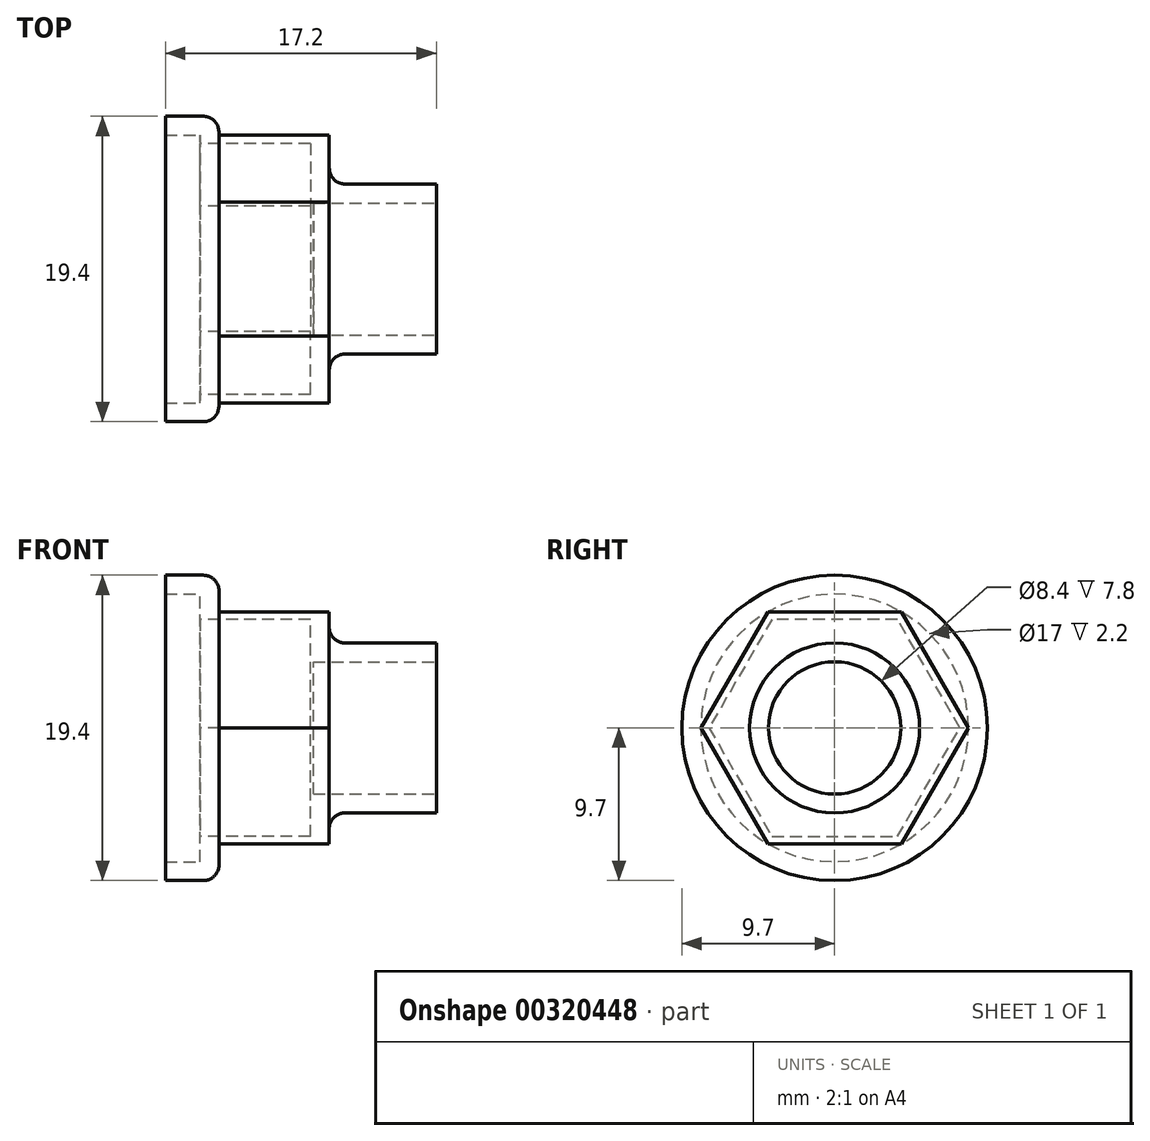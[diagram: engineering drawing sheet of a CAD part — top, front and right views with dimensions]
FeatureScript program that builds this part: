
annotation { "Feature Type Name" : "Feature", "Feature Type Description" : "" }
export const myFeature = defineFeature(function(context is Context, id is Id, definition is map)
    precondition{}
    {
        {
            var Q0;
            Q0=qCreatedBy(makeId("Top.planeOp"),FACE);
            var sketch = newSketch(context, id + "F0", { "sketchPlane" : qUnion([Q0])});
            skLineSegment(sketch, "E0", {"start": v(0, 6.7) * mm, "end": v(7, 6.7) * mm});
            skLineSegment(sketch, "E1", {"start": v(7, 6.7) * mm, "end": v(7, 4.2) * mm});
            skLineSegment(sketch, "E2", {"start": v(7, 4.2) * mm, "end": v(15, 4.2) * mm});
            skLineSegment(sketch, "E3", {"start": v(15, 4.2) * mm, "end": v(15, 4.2) * mm});
            skArc(sketch, "E4", {"start": v(19.2, 0) * mm, "mid": v(17.97, 2.97) * mm, "end": v(15, 4.2) * mm, "construction": true});
            skLineSegment(sketch, "E5", {"start": v(0, 6.7) * mm, "end": v(0, 8.5) * mm});
            skLineSegment(sketch, "E6", {"start": v(0, 8.5) * mm, "end": v(-2.2, 8.5) * mm});
            skLineSegment(sketch, "E7", {"start": v(19.2, 0) * mm, "end": v(0, 0) * mm, "construction": true});
            skLineSegment(sketch, "E8", {"start": v(-2.2, 8.5) * mm, "end": v(-2.2, 9.7) * mm});
            skLineSegment(sketch, "E9", {"start": v(-2.2, 9.7) * mm, "end": v(1.2, 9.7) * mm});
            skLineSegment(sketch, "E10", {"start": v(1.2, 9.7) * mm, "end": v(1.2, 8.5) * mm});
            skLineSegment(sketch, "E11", {"start": v(1.2, 8.5) * mm, "end": v(8.2, 8.5) * mm});
            skLineSegment(sketch, "E12", {"start": v(8.2, 8.5) * mm, "end": v(8.2, 5.4) * mm});
            skLineSegment(sketch, "E13", {"start": v(8.2, 5.4) * mm, "end": v(15, 5.4) * mm});
            skLineSegment(sketch, "E14", {"start": v(19.2, 0) * mm, "end": v(20.4, 0) * mm, "construction": true});
            skArc(sketch, "E15", {"start": v(20.4, 0) * mm, "mid": v(18.82, 3.82) * mm, "end": v(15, 5.4) * mm, "construction": true});
            skLineSegment(sketch, "E16", {"start": v(15, 4.2) * mm, "end": v(15, 5.4) * mm});
            skSolve(sketch);
        }
        {
            var Q0;
            Q0=qSketchRegion(id+"F0",true);
            var Q1;
            Q1=sQuery(id+"F0.wireOp",EDGE,"E7");
            revolve(context, id + "F1", {"entities" : qUnion([Q0]), "axis" : qUnion([Q1]), "revolveType" : RevolveType.FULL});
        }
        {
            var Q0;
            Q0=makeQuery(id+"F1.opRevolve","SWEPT_FACE",FACE,{"disambiguationData":[OSD([sQuery(id+"F0.wireOp",EDGE,"E5")])]});
            var sketch = newSketch(context, id + "F2", { "sketchPlane" : qUnion([Q0])});
            skCircle(sketch, "E17", {"center": v(0, 0) * mm, "radius": 6.9 * mm, "construction": true});
            skLineSegment(sketch, "E18.0", {"start": v(-3.98, 6.9) * mm, "end": v(3.98, 6.9) * mm});
            skLineSegment(sketch, "E18.1", {"start": v(3.98, 6.9) * mm, "end": v(7.97, 0) * mm});
            skLineSegment(sketch, "E18.2", {"start": v(7.97, 0) * mm, "end": v(3.98, -6.9) * mm});
            skLineSegment(sketch, "E18.3", {"start": v(3.98, -6.9) * mm, "end": v(-3.98, -6.9) * mm});
            skLineSegment(sketch, "E18.4", {"start": v(-3.98, -6.9) * mm, "end": v(-7.97, 0) * mm});
            skLineSegment(sketch, "E18.5", {"start": v(-7.97, 0) * mm, "end": v(-3.98, 6.9) * mm});
            skPoint(sketch, "E18.0.midPoint", {"position": v(0, 6.9) * mm});
            skSolve(sketch);
        }
        {
            var Q0;
            Q0=qSketchRegion(id+"F2",true);
            extrude(context, id + "F3", {"entities" : qUnion([Q0]), "operationType" : NewBodyOperationType.REMOVE, "oppositeDirection" : true, "depth" : 7 * mm});
        }
        {
            var Q0;
            Q0=makeQuery(id+"F1.opRevolve","SWEPT_FACE",FACE,{"disambiguationData":[OSD([sQuery(id+"F0.wireOp",EDGE,"E10")])]});
            var sketch = newSketch(context, id + "F4", { "sketchPlane" : qUnion([Q0])});
            skCircle(sketch, "E19.cCircle", {"center": v(0, 0) * mm, "radius": 7.36 * mm, "construction": true});
            skLineSegment(sketch, "E19.0", {"start": v(-4.25, 7.36) * mm, "end": v(4.25, 7.36) * mm});
            skLineSegment(sketch, "E19.1", {"start": v(4.25, 7.36) * mm, "end": v(8.5, 0) * mm});
            skLineSegment(sketch, "E19.2", {"start": v(8.5, 0) * mm, "end": v(4.25, -7.36) * mm});
            skLineSegment(sketch, "E19.3", {"start": v(4.25, -7.36) * mm, "end": v(-4.25, -7.36) * mm});
            skLineSegment(sketch, "E19.4", {"start": v(-4.25, -7.36) * mm, "end": v(-8.5, 0) * mm});
            skLineSegment(sketch, "E19.5", {"start": v(-8.5, 0) * mm, "end": v(-4.25, 7.36) * mm});
            skPoint(sketch, "E19.0.midPoint", {"position": v(0, 7.36) * mm});
            skCircle(sketch, "E20", {"center": v(0, 0) * mm, "radius": 10.14 * mm});
            skSolve(sketch);
        }
        {
            var Q0;
            Q0=qSketchRegion(id+"F4",true);
            extrude(context, id + "F5", {"entities" : qUnion([Q0]), "operationType" : NewBodyOperationType.REMOVE, "endBound" : BoundingType.THROUGH_ALL, "depth" : 25 * mm});
        }
        {
            var Q0;
            Q0=makeQuery(id+"F1.opRevolve","SWEPT_EDGE",EDGE,{"disambiguationData":[OSD([sQuery(id+"F0.wireOp",EDGE,"E12"),sQuery(id+"F0.wireOp",EDGE,"E13")])]});
            fillet(context, id + "F6", {"entities" : qUnion([Q0]), "radius" : 1 * mm, "tangentPropagation" : true, "allowEdgeOverflow" : false});
        }
        {
            var Q0;
            Q0=makeQuery(id+"F1.opRevolve","SWEPT_EDGE",EDGE,{"disambiguationData":[OSD([sQuery(id+"F0.wireOp",EDGE,"E9"),sQuery(id+"F0.wireOp",EDGE,"E10")])]});
            fillet(context, id + "F7", {"entities" : qUnion([Q0]), "radius" : 1 * mm, "tangentPropagation" : true, "allowEdgeOverflow" : false});
        }
        {
            var Q0;
            Q0=makeQuery(id+"F3.boolean.opBoolean","MERGE",FACE,{"derivedFrom":[makeQuery(id+"F1.opRevolve","SWEPT_FACE",FACE,{"disambiguationData":[OSD([sQuery(id+"F0.wireOp",EDGE,"E1")])]}),makeQuery(id+"F3.opExtrude","CAP_FACE",FACE,{"disambiguationData":[OSD([sQuery(id+"F2.wireOp",EDGE,"E18.0"),sQuery(id+"F2.wireOp",EDGE,"E18.1"),sQuery(id+"F2.wireOp",EDGE,"E18.2"),sQuery(id+"F2.wireOp",EDGE,"E18.3"),sQuery(id+"F2.wireOp",EDGE,"E18.4"),sQuery(id+"F2.wireOp",EDGE,"E18.5")])],"isStart":false})]});
            var sketch = newSketch(context, id + "F8", { "sketchPlane" : qUnion([Q0])});
            skCircle(sketch, "E21", {"center": v(0, 0) * mm, "radius": 4.2 * mm});
            skSolve(sketch);
        }
        {
            var Q0;
            Q0 = qSketchRegion(id + "F8", true);
            extrude(context, id + "F9", {"entities" : qUnion([Q0]), "operationType" : NewBodyOperationType.ADD, "oppositeDirection" : true, "depth" : 0.2 * mm});
        }
    });
